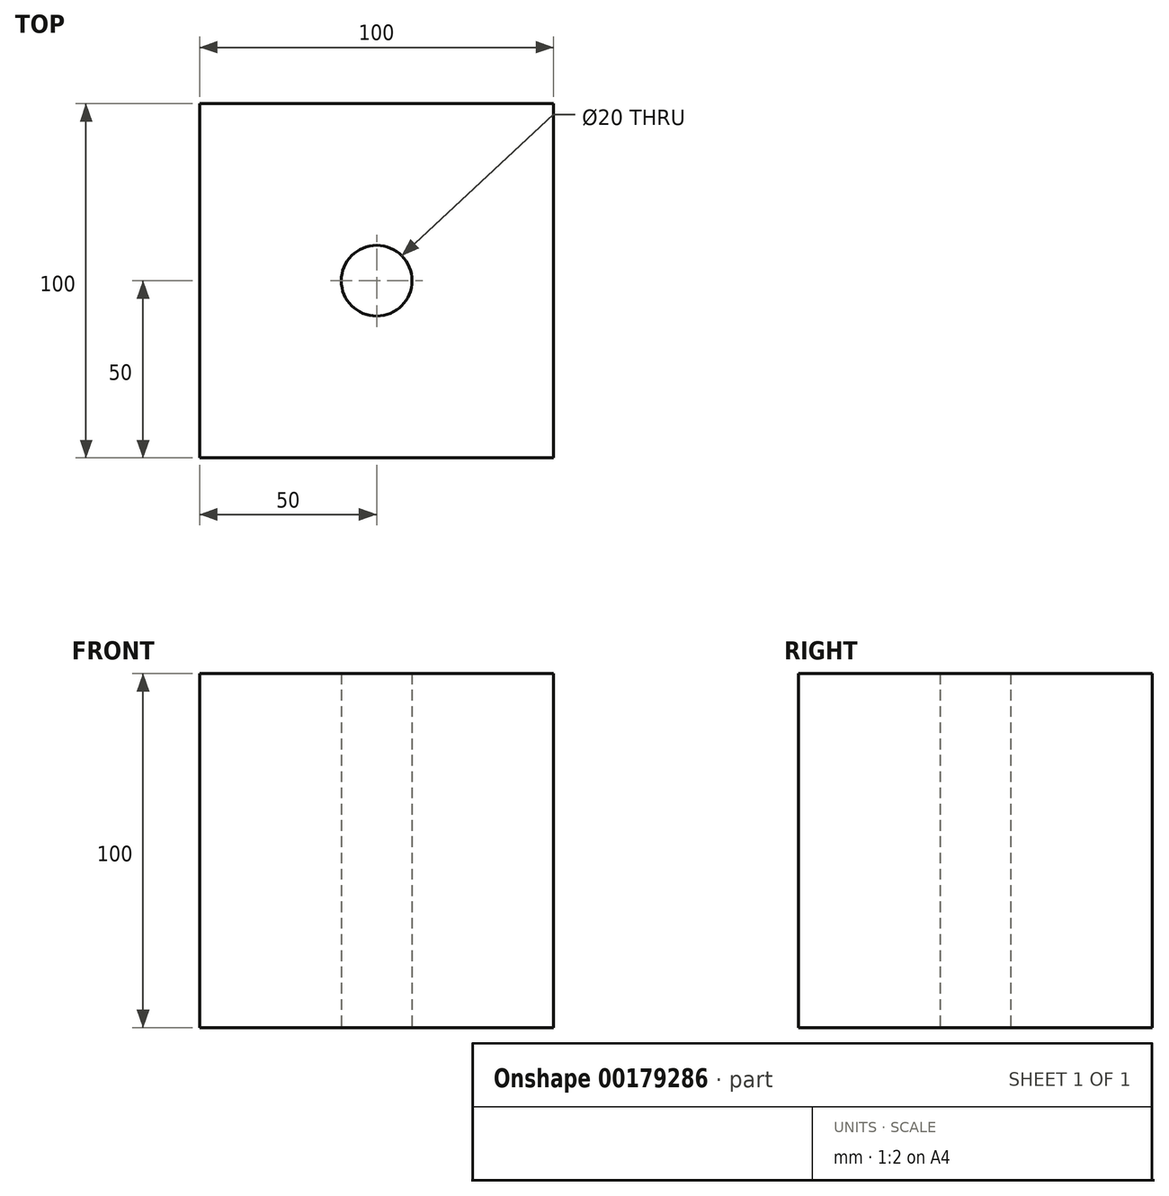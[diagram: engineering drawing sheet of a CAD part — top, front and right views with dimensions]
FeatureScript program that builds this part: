
annotation { "Feature Type Name" : "Feature", "Feature Type Description" : "" }
export const myFeature = defineFeature(function(context is Context, id is Id, definition is map)
    precondition{}
    {
        {
            var Q0;
            Q0=qCreatedBy(makeId("Top.planeOp"),FACE);
            var sketch = newSketch(context, id + "F0", { "sketchPlane" : qUnion([Q0])});
            skLineSegment(sketch, "E0", {"start": v(0, 0) * mm, "end": v(100, 0) * mm});
            skLineSegment(sketch, "E1", {"start": v(100, 0) * mm, "end": v(100, 100) * mm});
            skLineSegment(sketch, "E2", {"start": v(100, 100) * mm, "end": v(0, 100) * mm});
            skLineSegment(sketch, "E3", {"start": v(0, 100) * mm, "end": v(0, 0) * mm});
            skLineSegment(sketch, "E4", {"start": v(0, 50) * mm, "end": v(100, 50) * mm, "construction": true});
            skCircle(sketch, "E5", {"center": v(50, 50) * mm, "radius": 10 * mm});
            skSolve(sketch);
        }
        {
            var Q0;
            Q0=makeQuery(id+"F0.imprint","IMPRINT",FACE,{"disambiguationData":[TD([[makeQuery(id+"F0.imprint","IMPRINT",EDGE,{"derivedFrom":sQuery(id+"F0.wireOp",EDGE,"E0")}),1.0]])]});
            extrude(context, id + "F1", {"entities" : qUnion([Q0]), "depth" : 100 * mm});
        }
    });
